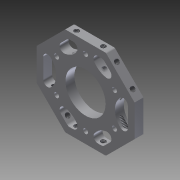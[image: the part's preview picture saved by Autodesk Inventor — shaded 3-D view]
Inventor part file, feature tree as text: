
AUTODESK INVENTOR PART (.ipt)
format: ipt  version: 2012 (Build 160160000, 160)  size: 349,184 bytes
history: native  units: in
note: dims shown in document units (in); Inventor stores cm internally (conversion verified against a paired STEP export)
features: thread x12, sketch x7, extrude x7, fillet x2
ambient origin geometry x8: Origin, YZ Plane, XZ Plane, XY Plane, X Axis, Y Axis, Z Axis, Center Point
bodies: Solid1 (feature_tree)
feature tree (28):
  sketch  "Sketch1"  dims[d0=2.75in d1=2.5in d2=1.375in d3=1.25in]
  extrude  "Extrusion1"  Depth=2.5in
  fillet  "Fillet1"  Radius=1.375in
  fillet  "Fillet2"  Radius=1.25in
  extrude  "Extrusion3"  TaperAngle=45.0deg  [1 undecoded]
  sketch  "Sketch3"  dims[d8=45.0deg d10=0.136in]
  extrude  "Extrusion4"  Depth=0.136in
  extrude  "Extrusion5"  Depth=1.125in
  extrude  "Extrusion6"  Depth=0.1875in
  extrude  "Extrusion7"  Depth=0.1875in
  extrude  "Extrusion8"  Depth=0.1875in
  thread  "Thread1"  [1 undecoded]
  thread  "Thread2"  [1 undecoded]
  thread  "Thread3"  [1 undecoded]
  thread  "Thread4"  [1 undecoded]
  thread  "Thread5"  [1 undecoded]
  thread  "Thread6"  [1 undecoded]
  thread  "Thread7"  [1 undecoded]
  thread  "Thread8"  [1 undecoded]
  thread  "Thread9"  [1 undecoded]
  thread  "Thread10"  [1 undecoded]
  thread  "Thread11"  [1 undecoded]
  thread  "Thread12"  [1 undecoded]
  sketch  "Sketch2"  dims[d6=45.0deg d7=45.0deg]
  sketch  "Sketch4"  dims[d11=0.938in d18=1.125in]
  sketch  "Sketch6"  dims[d20=2.3622in d22=360.0deg d24=0.1875in]
  sketch  "Sketch7"  dims[d25=0.1875in d26=0.1875in]
  sketch  "Sketch8"  dims[d27=0.1875in d28=0.1875in d29=0.1875in d30=0.1875in d32=0.1875in d33=0.5in d34=0.25in d35=0.0in d38=0.125in d39=0.125in d40=0.0625in d41=0.75in d42=0.1687in d43=0.1687in d44=0.136in d45=0.125in d46=0.25in d47=0.0in d48=0.125in d49=0.136in d50=0.25in d51=0.625in d52=0.125in d53=0.25in d54=0.625in d55=0.136in d56=0.625in d57=0.0in d58=0.625in d59=0.0in d61=0.75in d62=0.136in d63=0.1687in d64=0.1687in d65=0.125in d66=0.25in d67=0.0in d68=0.25in d69=0.625in d70=0.136in d71=0.125in d72=0.625in d73=0.0in d74=0.25in d75=0.125in d76=0.625in d77=0.136in d78=0.625in d79=0.0in d80=1.0in d81=0.0in d82=1.0in d83=0.0in d84=1.0in d85=0.0in d86=1.0in d87=0.0in d88=1.0in d89=0.0in d90=1.0in d91=0.0in d92=1.0in d93=0.0in d94=1.0in d95=0.0in d96=1.0in d97=0.0in d98=1.0in d99=0.0in d100=1.0in d101=0.0in d102=1.0in d103=0.0in]
note: 13 required parameter values undecoded (feature->parameter linkage not recoverable at this tier; creation-order binding heuristic only, values carry confidence <= 0.55)
